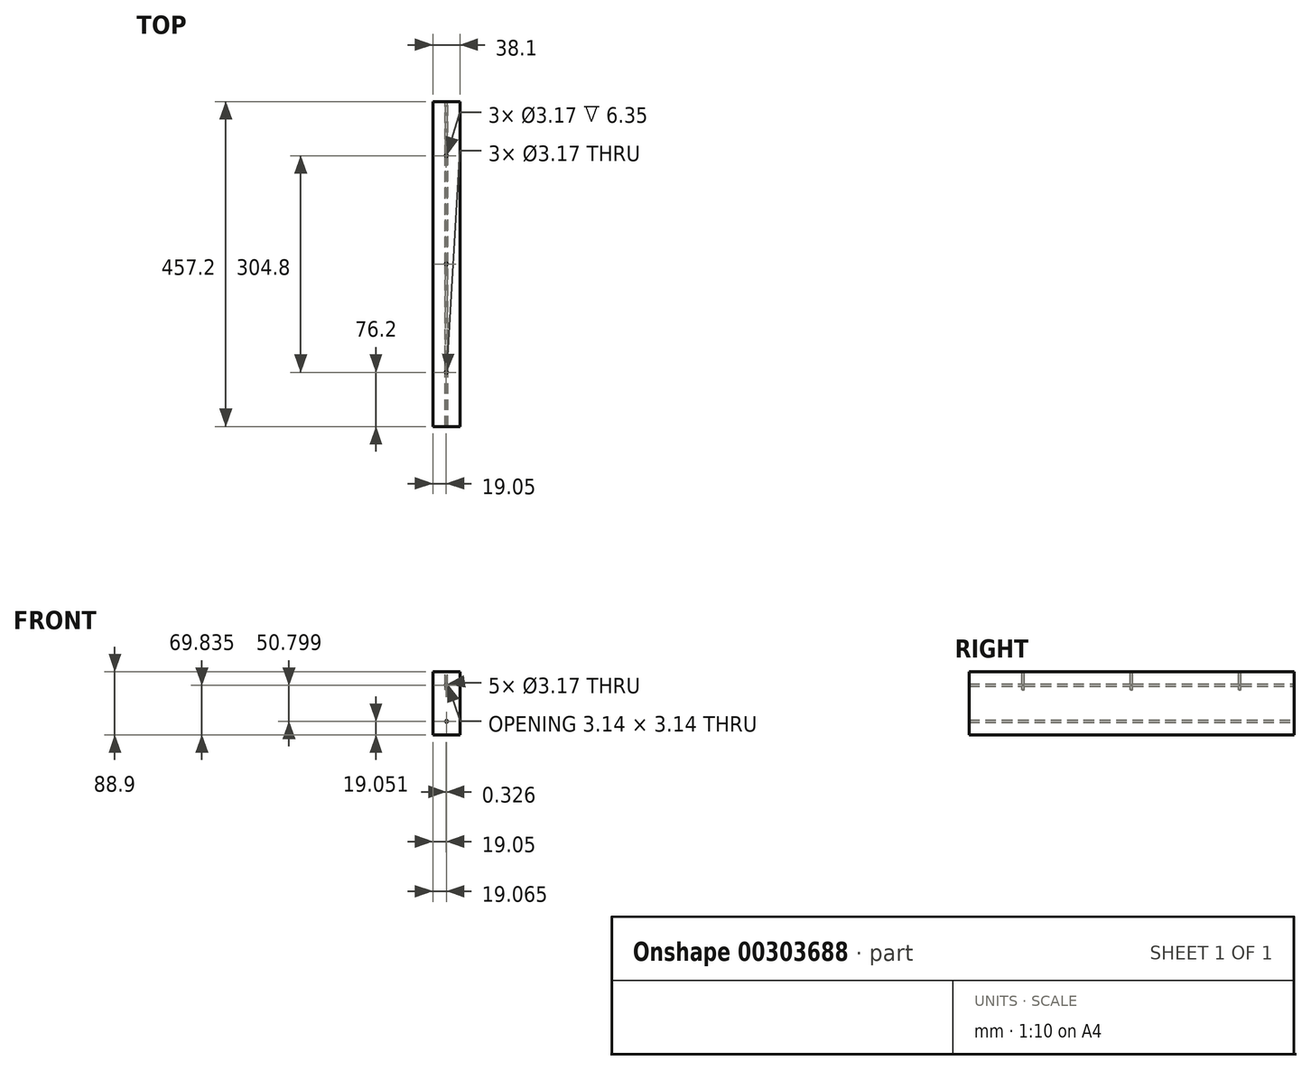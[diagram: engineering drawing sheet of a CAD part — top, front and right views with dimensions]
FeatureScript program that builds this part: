
annotation { "Feature Type Name" : "Feature", "Feature Type Description" : "" }
export const myFeature = defineFeature(function(context is Context, id is Id, definition is map)
    precondition{}
    {
        {
            var Q0;
            Q0=qCreatedBy(makeId("Front.planeOp"),FACE);
            var sketch = newSketch(context, id + "F0", { "sketchPlane" : qUnion([Q0])});
            skLineSegment(sketch, "E0.bottom", {"start": v(0, 0) * mm, "end": v(38.1, 0) * mm});
            skLineSegment(sketch, "E0.top", {"start": v(0, -88.9) * mm, "end": v(38.1, -88.9) * mm});
            skLineSegment(sketch, "E0.left", {"start": v(0, 0) * mm, "end": v(0, -88.9) * mm});
            skLineSegment(sketch, "E0.right", {"start": v(38.1, 0) * mm, "end": v(38.1, -88.9) * mm});
            skSolve(sketch);
        }
        {
            var Q0;
            Q0 = qSketchRegion(id + "F0", true);
            extrude(context, id + "F1", {"entities" : qUnion([Q0]), "depth" : 457.2 * mm});
        }
        {
            var Q0;
            Q0=qCreatedBy(makeId("Front.planeOp"),FACE);
            var sketch = newSketch(context, id + "F2", { "sketchPlane" : qUnion([Q0])});
            skCircle(sketch, "E1", {"center": v(19.05, -19.05) * mm, "radius": 1.59 * mm});
            skCircle(sketch, "E2.1.0.0", {"center": v(19.38, -69.85) * mm, "radius": 1.59 * mm});
            skLineSegment(sketch, "E2.direction1", {"start": v(19.05, -19.05) * mm, "end": v(19.38, -69.85) * mm, "construction": true});
            skSolve(sketch);
        }
        {
            var Q0;
            Q0 = qSketchRegion(id + "F2", true);
            extrude(context, id + "F3", {"entities" : qUnion([Q0]), "operationType" : NewBodyOperationType.REMOVE, "depth" : 457.2 * mm});
        }
        {
            var Q0;
            Q0=qCreatedBy(makeId("Top.planeOp"),FACE);
            var sketch = newSketch(context, id + "F4", { "sketchPlane" : qUnion([Q0])});
            skCircle(sketch, "E3", {"center": v(19.05, -76.2) * mm, "radius": 1.59 * mm});
            skCircle(sketch, "E4.1.0.0", {"center": v(19.05, -228.6) * mm, "radius": 1.59 * mm});
            skCircle(sketch, "E4.2.0.0", {"center": v(19.05, -381) * mm, "radius": 1.59 * mm});
            skLineSegment(sketch, "E4.direction1", {"start": v(19.05, -76.2) * mm, "end": v(19.05, -228.6) * mm, "construction": true});
            skSolve(sketch);
        }
        {
            var Q0;
            Q0 = qSketchRegion(id + "F4", true);
            extrude(context, id + "F5", {"entities" : qUnion([Q0]), "operationType" : NewBodyOperationType.REMOVE, "oppositeDirection" : true, "depth" : 25.4 * mm});
        }
    });
